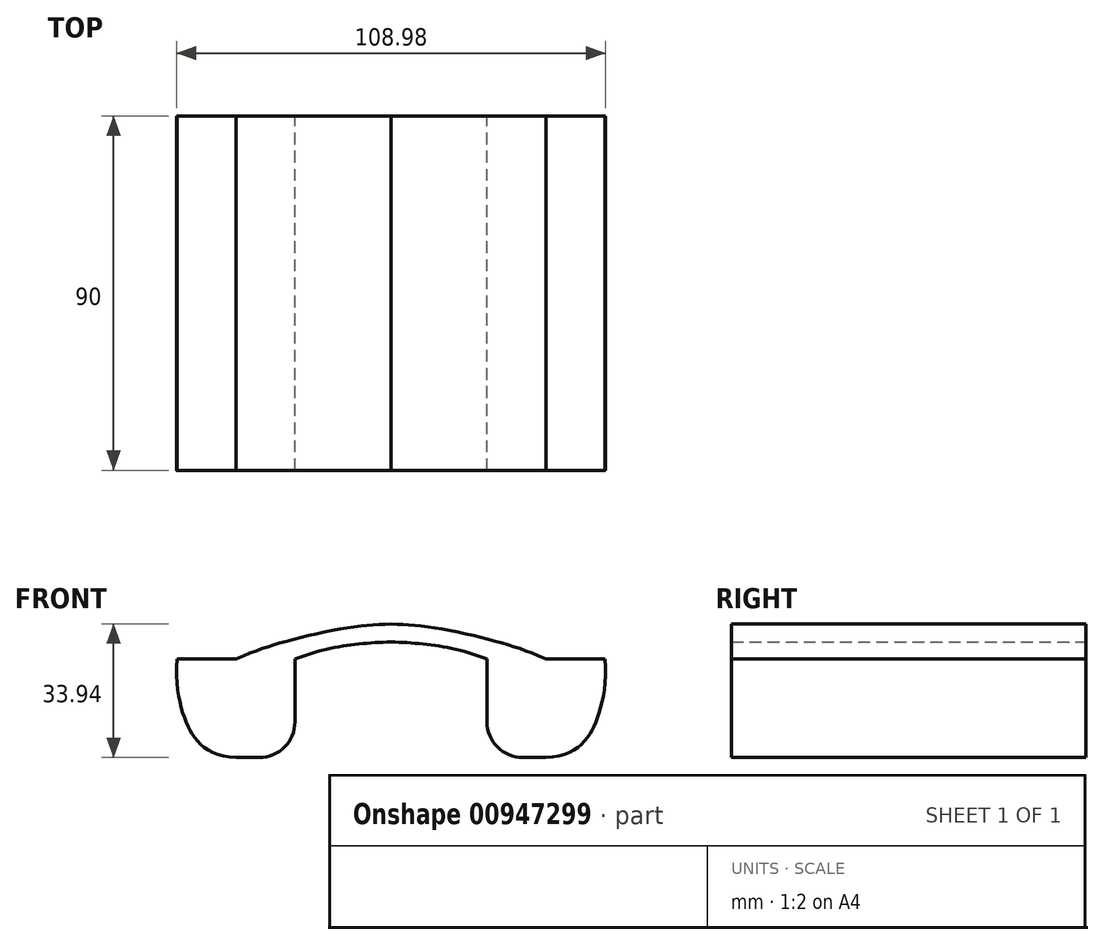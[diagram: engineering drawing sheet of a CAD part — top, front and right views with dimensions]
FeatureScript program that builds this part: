
annotation { "Feature Type Name" : "Feature", "Feature Type Description" : "" }
export const myFeature = defineFeature(function(context is Context, id is Id, definition is map)
    precondition{}
    {
        {
            var Q0;
            Q0=qCreatedBy(makeId("Front.planeOp"),FACE);
            var sketch = newSketch(context, id + "F0", { "sketchPlane" : qUnion([Q0])});
            skLineSegment(sketch, "E0", {"start": v(0, 0) * mm, "end": v(0, 44.19) * mm, "construction": true});
            skLineSegment(sketch, "E1", {"start": v(0, 0) * mm, "end": v(0, -40.13) * mm, "construction": true});
            skLineSegment(sketch, "E2", {"start": v(39.4, -6.95) * mm, "end": v(0, 0) * mm, "construction": true});
            skLineSegment(sketch, "E3", {"start": v(39.4, -6.95) * mm, "end": v(24.4, -6.95) * mm});
            skLineSegment(sketch, "E4", {"start": v(39.4, -6.95) * mm, "end": v(54.4, -6.95) * mm});
            skLineSegment(sketch, "E5", {"start": v(39.4, -6.95) * mm, "end": v(39.4, -31.95) * mm, "construction": true});
            skFitSpline(sketch, "E6", {"points": [v(54.4, -6.95) * mm, v(53.16, -19.71) * mm, v(50.87, -25.43) * mm, v(47.44, -29.4) * mm, v(39.4, -31.95) * mm], "startDerivative": vector(3.47, -52.05) * mm, "endDerivative": vector(-40.17, 0.6) * mm});
            skLineSegment(sketch, "E7", {"start": v(24.4, -6.95) * mm, "end": v(24.4, -22.95) * mm});
            skLineSegment(sketch, "E8", {"start": v(33.4, -31.95) * mm, "end": v(39.4, -31.95) * mm});
            skPoint(sketch, "E9.visualSharp", {"position": v(24.4, -31.95) * mm});
            skArc(sketch, "E9.filletArc", {"start": v(24.4, -22.95) * mm, "mid": v(27.03, -29.3) * mm, "end": v(33.4, -31.95) * mm});
            skLineSegment(sketch, "E10.MirrorCS", {"start": v(-39.4, -6.95) * mm, "end": v(0, 0) * mm, "construction": true});
            skLineSegment(sketch, "E11.MirrorCS", {"start": v(-39.4, -6.95) * mm, "end": v(-54.4, -6.95) * mm});
            skLineSegment(sketch, "E12.MirrorCS", {"start": v(-39.4, -6.95) * mm, "end": v(-24.4, -6.95) * mm});
            skLineSegment(sketch, "E13.MirrorCS", {"start": v(-24.4, -6.95) * mm, "end": v(-24.4, -22.95) * mm});
            skFitSpline(sketch, "E14.MirrorCS", {"points": [v(-54.4, -6.95) * mm, v(-53.16, -19.71) * mm, v(-50.87, -25.43) * mm, v(-47.44, -29.4) * mm, v(-39.4, -31.95) * mm], "startDerivative": vector(-3.47, -52.05) * mm, "endDerivative": vector(40.17, 0.6) * mm});
            skLineSegment(sketch, "E15.MirrorCS", {"start": v(-39.4, -6.95) * mm, "end": v(-39.4, -31.95) * mm, "construction": true});
            skLineSegment(sketch, "E16.MirrorCS", {"start": v(-33.4, -31.95) * mm, "end": v(-39.4, -31.95) * mm});
            skArc(sketch, "E17.MirrorCS", {"start": v(-24.4, -22.95) * mm, "mid": v(-27.03, -29.3) * mm, "end": v(-33.4, -31.95) * mm});
            skPoint(sketch, "E18.1.internal.snap0", {"position": v(19.7, -3.47) * mm});
            skFitSpline(sketch, "E18", {"points": [v(24.4, -6.95) * mm, v(11.07, -3.47) * mm, v(0, -2.61) * mm], "startDerivative": vector(-26.63, 10.14) * mm, "endDerivative": vector(-24.07, 0.86) * mm});
            skFitSpline(sketch, "E19", {"points": [v(39.4, -6.95) * mm, v(27.6, -2.74) * mm, v(11.07, 1.01) * mm, v(0, 2) * mm], "startDerivative": vector(-46.27, 20.1) * mm, "endDerivative": vector(-34.77, 2.34) * mm});
            skFitSpline(sketch, "E20.MirrorCS", {"points": [v(-24.4, -6.95) * mm, v(-11.07, -3.47) * mm, v(0, -2.61) * mm], "startDerivative": vector(26.63, 10.14) * mm, "endDerivative": vector(24.07, 0.86) * mm});
            skFitSpline(sketch, "E21.MirrorCS", {"points": [v(-39.4, -6.95) * mm, v(-27.6, -2.74) * mm, v(-11.07, 1.01) * mm, v(0, 2) * mm], "startDerivative": vector(46.27, 20.1) * mm, "endDerivative": vector(34.77, 2.34) * mm});
            skSolve(sketch);
        }
        {
            var Q0;
            Q0 = qSketchRegion(id + "F0", true);
            extrude(context, id + "F1", {"entities" : qUnion([Q0]), "depth" : 90 * mm, "offsetDistance" : 25 * mm});
        }
        {
            var Q0;
            Q0=qCreatedBy(makeId("Front.planeOp"),FACE);
            cPlane(context, id + "F2", {"entities" : qUnion([Q0]), "cplaneType" : CPlaneType.OFFSET, "offset" : 90 * mm, "width" : 150 * mm, "height" : 150 * mm});
        }
    });
